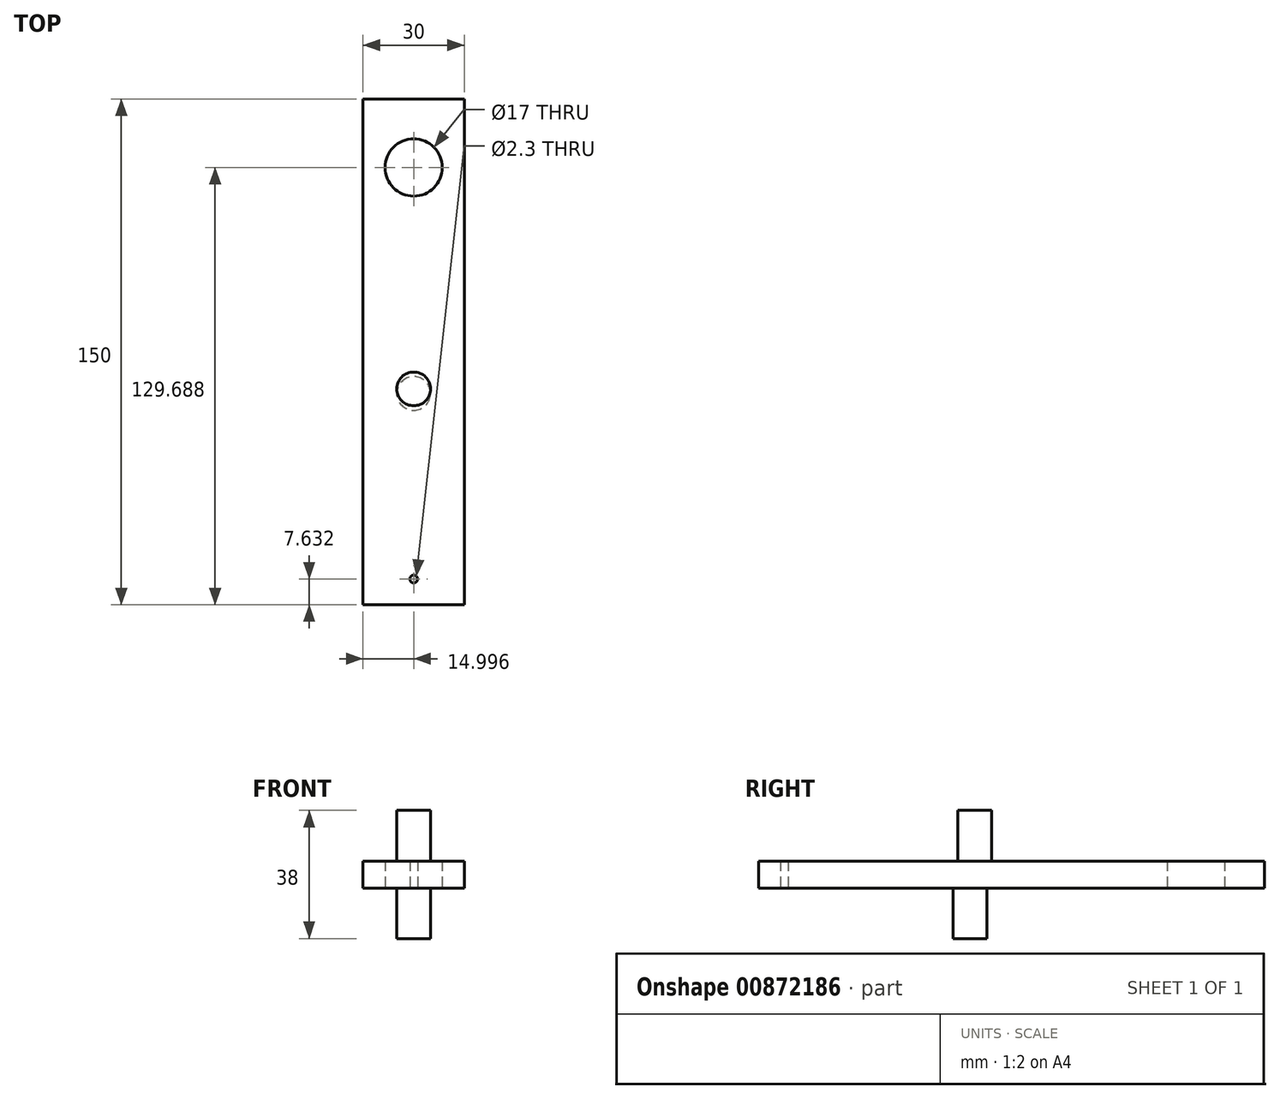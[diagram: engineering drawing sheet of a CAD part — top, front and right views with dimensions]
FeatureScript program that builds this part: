
annotation { "Feature Type Name" : "Feature", "Feature Type Description" : "" }
export const myFeature = defineFeature(function(context is Context, id is Id, definition is map)
    precondition{}
    {
        {
            var Q0;
            Q0=qCreatedBy(makeId("Top.planeOp"),FACE);
            var sketch = newSketch(context, id + "F0", { "sketchPlane" : qUnion([Q0])});
            skLineSegment(sketch, "E0.bottom", {"start": v(3.12, 0) * mm, "end": v(33.12, 0) * mm});
            skLineSegment(sketch, "E0.top", {"start": v(3.12, -150) * mm, "end": v(33.12, -150) * mm});
            skLineSegment(sketch, "E0.left", {"start": v(3.12, 0) * mm, "end": v(3.12, -150) * mm});
            skLineSegment(sketch, "E0.right", {"start": v(33.12, 0) * mm, "end": v(33.12, -150) * mm});
            skLineSegment(sketch, "E1", {"start": v(18.12, 0) * mm, "end": v(18.12, -150) * mm, "construction": true});
            skCircle(sketch, "E2", {"center": v(18.12, -20.31) * mm, "radius": 8.5 * mm});
            skSolve(sketch);
        }
        {
            var Q0;
            Q0=makeQuery(id+"F0.imprint","IMPRINT",FACE,{"disambiguationData":[TD([[makeQuery(id+"F0.imprint","IMPRINT",EDGE,{"derivedFrom":sQuery(id+"F0.wireOp",EDGE,"E0.bottom")}),-1.0]])]});
            extrude(context, id + "F1", {"entities" : qUnion([Q0]), "depth" : 8 * mm, "offsetDistance" : 25 * mm});
        }
        {
            var Q0;
            Q0=makeQuery(id+"F1.opExtrude","CAP_FACE",FACE,{"disambiguationData":[OSD([sQuery(id+"F0.wireOp",EDGE,"E0.bottom"),sQuery(id+"F0.wireOp",EDGE,"E0.top"),sQuery(id+"F0.wireOp",EDGE,"E0.left"),sQuery(id+"F0.wireOp",EDGE,"E0.right"),sQuery(id+"F0.wireOp",EDGE,"E2")])],"isStart":false});
            var sketch = newSketch(context, id + "F2", { "sketchPlane" : qUnion([Q0])});
            skLineSegment(sketch, "E3", {"start": v(18.12, 0) * mm, "end": v(18.12, -150) * mm, "construction": true});
            skCircle(sketch, "E4", {"center": v(18.12, -85.97) * mm, "radius": 5 * mm});
            skLineSegment(sketch, "E5", {"start": v(18.12, -90.97) * mm, "end": v(18.12, -150) * mm, "construction": true});
            skSolve(sketch);
        }
        {
            var Q0;
            Q0 = qSketchRegion(id + "F2", true);
            extrude(context, id + "F3", {"entities" : qUnion([Q0]), "operationType" : NewBodyOperationType.ADD, "depth" : 15 * mm, "offsetDistance" : 25 * mm});
        }
        {
            var Q0;
            Q0=makeQuery(id+"F1.opExtrude","CAP_FACE",FACE,{"disambiguationData":[OSD([sQuery(id+"F0.wireOp",EDGE,"E0.bottom"),sQuery(id+"F0.wireOp",EDGE,"E0.top"),sQuery(id+"F0.wireOp",EDGE,"E0.left"),sQuery(id+"F0.wireOp",EDGE,"E0.right"),sQuery(id+"F0.wireOp",EDGE,"E2")])],"isStart":true});
            var sketch = newSketch(context, id + "F4", { "sketchPlane" : qUnion([Q0])});
            skLineSegment(sketch, "E6", {"start": v(18.12, 0) * mm, "end": v(18.12, 150) * mm, "construction": true});
            skLineSegment(sketch, "E7", {"start": v(18.12, 150) * mm, "end": v(18.12, 87.32) * mm, "construction": true});
            skCircle(sketch, "E8", {"center": v(18.12, 87.32) * mm, "radius": 5 * mm});
            skSolve(sketch);
        }
        {
            var Q0;
            Q0=makeQuery(id+"F4.imprint","IMPRINT",FACE,{"disambiguationData":[TD([[makeQuery(id+"F4.imprint","IMPRINT",EDGE,{"derivedFrom":sQuery(id+"F4.wireOp",EDGE,"E8")}),1.0]])]});
            extrude(context, id + "F5", {"entities" : qUnion([Q0]), "operationType" : NewBodyOperationType.ADD, "depth" : 15 * mm, "offsetDistance" : 25 * mm});
        }
        {
            var Q0;
            Q0=makeQuery(id+"F1.opExtrude","CAP_FACE",FACE,{"disambiguationData":[OSD([sQuery(id+"F0.wireOp",EDGE,"E0.bottom"),sQuery(id+"F0.wireOp",EDGE,"E0.top"),sQuery(id+"F0.wireOp",EDGE,"E0.left"),sQuery(id+"F0.wireOp",EDGE,"E0.right"),sQuery(id+"F0.wireOp",EDGE,"E2")])],"isStart":true});
            var sketch = newSketch(context, id + "F6", { "sketchPlane" : qUnion([Q0])});
            skLineSegment(sketch, "E9", {"start": v(18.12, 150) * mm, "end": v(18.12, 0) * mm, "construction": true});
            skCircle(sketch, "E10", {"center": v(18.12, 142.37) * mm, "radius": 1.15 * mm});
            skSolve(sketch);
        }
        {
            var Q0;
            Q0=makeQuery(id+"F6.imprint","IMPRINT",FACE,{"disambiguationData":[TD([[makeQuery(id+"F6.imprint","IMPRINT",EDGE,{"derivedFrom":sQuery(id+"F6.wireOp",EDGE,"E10")}),1.0]])]});
            var Q1;
            Q1=sQuery(id+"F6.wireOp",EDGE,"E10");
            extrude(context, id + "F7", {"entities" : qUnion([Q0]), "operationType" : NewBodyOperationType.REMOVE, "surfaceEntities" : qUnion([Q1]), "oppositeDirection" : true, "depth" : 25 * mm, "offsetDistance" : 25 * mm});
        }
    });
